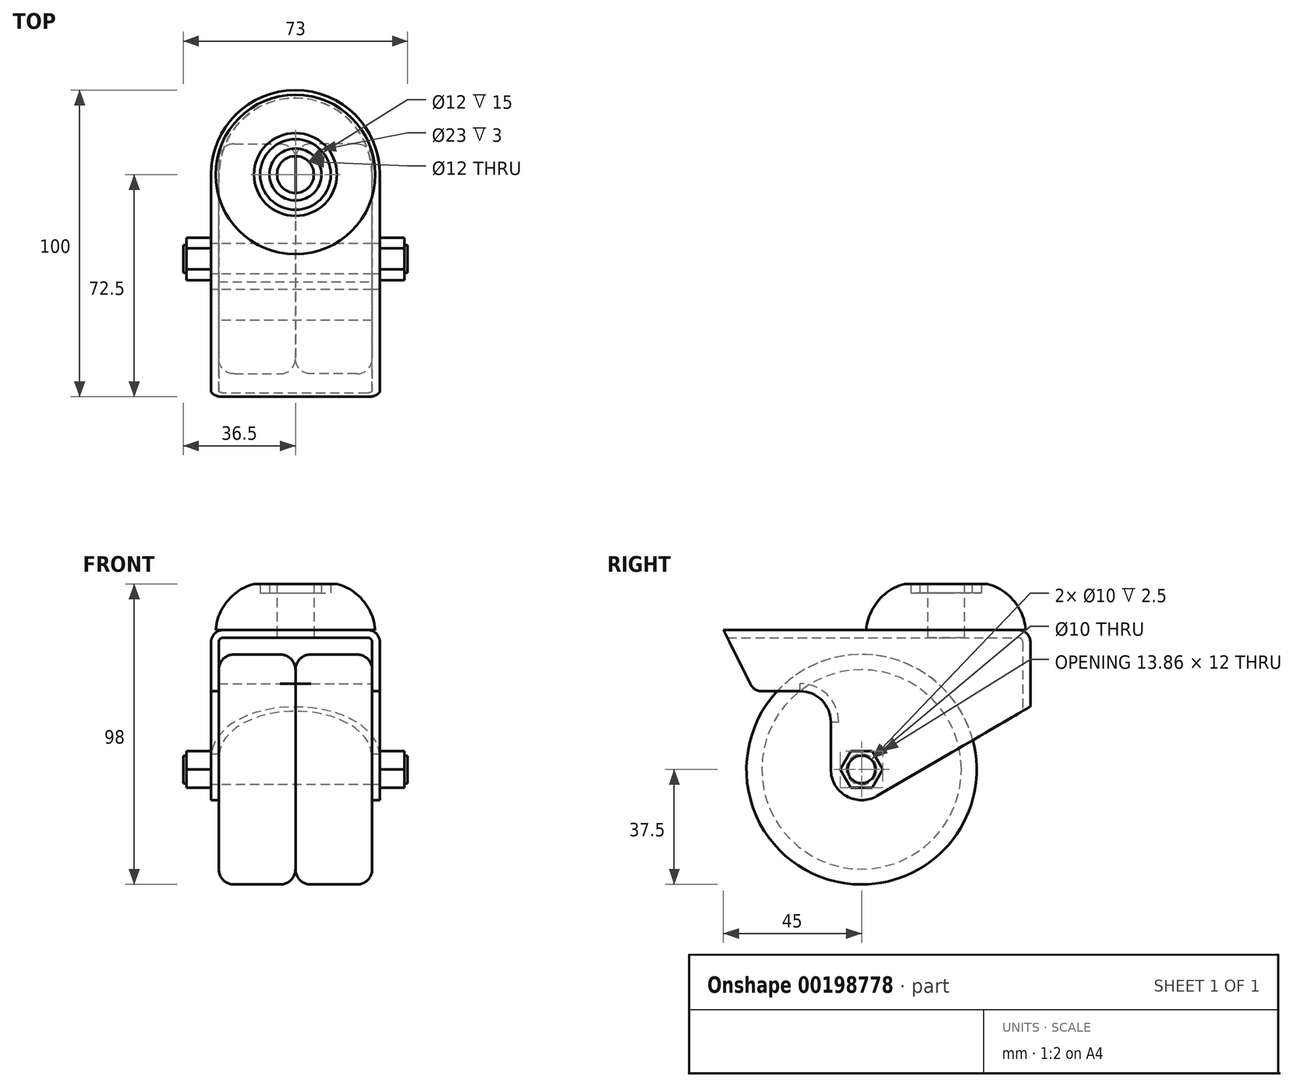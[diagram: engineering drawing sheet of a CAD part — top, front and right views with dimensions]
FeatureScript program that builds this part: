
annotation { "Feature Type Name" : "Feature", "Feature Type Description" : "" }
export const myFeature = defineFeature(function(context is Context, id is Id, definition is map)
    precondition{}
    {
        {
            var Q0;
            Q0=qCreatedBy(makeId("Right.planeOp"),FACE);
            var sketch = newSketch(context, id + "F0", { "sketchPlane" : qUnion([Q0])});
            skCircle(sketch, "E0", {"center": v(0, 0) * mm, "radius": 37.5 * mm});
            skCircle(sketch, "E1", {"center": v(0, 0) * mm, "radius": 5 * mm});
            skSolve(sketch);
        }
        {
            var Q0;
            Q0=qSketchRegion(id+"F0",true);
            extrude(context, id + "F1", {"entities" : qUnion([Q0]), "depth" : 25 * mm});
        }
        {
            var Q0;
            Q0=makeQuery(id+"F1.opExtrude","CAP_EDGE",EDGE,{"disambiguationData":[OSD([sQuery(id+"F0.wireOp",EDGE,"E0")])],"isStart":true});
            var Q1;
            Q1=makeQuery(id+"F1.opExtrude","CAP_EDGE",EDGE,{"disambiguationData":[OSD([sQuery(id+"F0.wireOp",EDGE,"E0")])],"isStart":false});
            fillet(context, id + "F2", {"entities" : qUnion([Q0, Q1]), "radius" : 5 * mm, "tangentPropagation" : true, "allowEdgeOverflow" : false});
        }
        {
            var Q0;
            Q0=makeQuery(id+"F1.opExtrude","SWEPT_BODY",BODY,{"disambiguationData":[OSD([sQuery(id+"F0.wireOp",EDGE,"E0")])]});
            var Q1;
            Q1=qCreatedBy(makeId("Right.planeOp"),FACE);
            mirror(context, id + "F3", {"operationType" : NewBodyOperationType.ADD, "entities" : qUnion([Q0]), "mirrorPlane" : qUnion([Q1])});
        }
        {
            var Q0;
            Q0=qCreatedBy(makeId("Right.planeOp"),FACE);
            var sketch = newSketch(context, id + "F4", { "sketchPlane" : qUnion([Q0])});
            skCircle(sketch, "E2.0", {"center": v(0, 0) * mm, "radius": 5 * mm});
            skArc(sketch, "E3", {"start": v(-10, 0) * mm, "mid": v(-4.98, -8.67) * mm, "end": v(5.04, -8.64) * mm});
            skLineSegment(sketch, "E4", {"start": v(0, -37.5) * mm, "end": v(0, 45.5) * mm, "construction": true});
            skLineSegment(sketch, "E5", {"start": v(-45, 45.5) * mm, "end": v(55, 45.5) * mm});
            skLineSegment(sketch, "E6", {"start": v(-10, 0) * mm, "end": v(-10, 25.5) * mm});
            skLineSegment(sketch, "E7", {"start": v(-10, 25.5) * mm, "end": v(-35, 25.5) * mm});
            skLineSegment(sketch, "E8", {"start": v(-35, 25.5) * mm, "end": v(-45, 45.5) * mm});
            skLineSegment(sketch, "E9", {"start": v(5.04, -8.64) * mm, "end": v(55, 20.5) * mm});
            skLineSegment(sketch, "E10", {"start": v(55, 20.5) * mm, "end": v(55, 45.5) * mm});
            skSolve(sketch);
        }
        {
            var Q0;
            Q0=qSketchRegion(id+"F4",true);
            extrude(context, id + "F5", {"entities" : qUnion([Q0]), "depth" : 55 * mm, "symmetric" : true});
        }
        {
            var Q0;
            Q0=makeQuery(id+"F5.opExtrude","CAP_EDGE",EDGE,{"disambiguationData":[OSD([sQuery(id+"F4.wireOp",EDGE,"E10")])],"isStart":false});
            var Q1;
            Q1=makeQuery(id+"F5.opExtrude","CAP_EDGE",EDGE,{"disambiguationData":[OSD([sQuery(id+"F4.wireOp",EDGE,"E10")])],"isStart":true});
            fillet(context, id + "F6", {"entities" : qUnion([Q0, Q1]), "radius" : (55 / 2) * mm, "tangentPropagation" : true, "allowEdgeOverflow" : false});
        }
        {
            var Q0;
            Q0=makeQuery(id+"F5.opExtrude","SWEPT_EDGE",EDGE,{"disambiguationData":[OSD([sQuery(id+"F4.wireOp",EDGE,"E6"),sQuery(id+"F4.wireOp",EDGE,"E7")])]});
            fillet(context, id + "F7", {"entities" : qUnion([Q0]), "radius" : 10 * mm, "tangentPropagation" : true, "allowEdgeOverflow" : false});
        }
        {
            var Q0;
            Q0=makeQuery(id+"F5.opExtrude","CAP_EDGE",EDGE,{"disambiguationData":[OSD([sQuery(id+"F4.wireOp",EDGE,"E5")])],"isStart":false});
            var Q1;
            Q1=makeQuery(id+"F5.opExtrude","SWEPT_EDGE",EDGE,{"disambiguationData":[OSD([sQuery(id+"F4.wireOp",EDGE,"E7"),sQuery(id+"F4.wireOp",EDGE,"E8")])]});
            fillet(context, id + "F8", {"entities" : qUnion([Q0, Q1]), "radius" : 4 * mm, "tangentPropagation" : true, "allowEdgeOverflow" : false});
        }
        {
            var Q0;
            Q0=makeQuery(id+"F5.opExtrude","SWEPT_FACE",FACE,{"disambiguationData":[OSD([sQuery(id+"F4.wireOp",EDGE,"E8")])]});
            var Q1;
            Q1=makeQuery(id+"F8.opFillet","BLEND_FACE",FACE,{"disambiguationData":[OSD([sQuery(id+"F4.wireOp",EDGE,"E7"),sQuery(id+"F4.wireOp",EDGE,"E8")])]});
            var Q2;
            Q2=makeQuery(id+"F5.opExtrude","SWEPT_FACE",FACE,{"disambiguationData":[OSD([sQuery(id+"F4.wireOp",EDGE,"E7")])]});
            var Q3;
            Q3=makeQuery(id+"F5.opExtrude","SWEPT_FACE",FACE,{"disambiguationData":[OSD([sQuery(id+"F4.wireOp",EDGE,"E6")])]});
            var Q4;
            Q4=makeQuery(id+"F5.opExtrude","SWEPT_FACE",FACE,{"disambiguationData":[OSD([sQuery(id+"F4.wireOp",EDGE,"E3")])]});
            var Q5;
            Q5=makeQuery(id+"F5.opExtrude","SWEPT_FACE",FACE,{"disambiguationData":[OSD([sQuery(id+"F4.wireOp",EDGE,"E2.0")])]});
            var Q6;
            Q6=makeQuery(id+"F5.opExtrude","SWEPT_FACE",FACE,{"disambiguationData":[OSD([sQuery(id+"F4.wireOp",EDGE,"E9")])]});
            shell(context, id + "F9", {"entities" : qUnion([Q0, Q1, Q2, Q3, Q4, Q5, Q6]), "thickness" : 2.5 * mm});
        }
        {
            var Q0;
            Q0=qCreatedBy(makeId("Right.planeOp"),FACE);
            var sketch = newSketch(context, id + "F10", { "sketchPlane" : qUnion([Q0])});
            skLineSegment(sketch, "E11.0", {"start": v(27.5, 45.5) * mm, "end": v(51, 45.5) * mm, "construction": true});
            skLineSegment(sketch, "E12", {"start": v(27.5, 45.5) * mm, "end": v(27.5, 60.5) * mm, "construction": true});
            skLineSegment(sketch, "E13.0", {"start": v(33.5, 45.5) * mm, "end": v(33.5, 60.5) * mm});
            skLineSegment(sketch, "E14", {"start": v(33.5, 60.5) * mm, "end": v(36, 60.5) * mm});
            skLineSegment(sketch, "E15", {"start": v(36, 60.5) * mm, "end": v(36, 57.5) * mm});
            skLineSegment(sketch, "E16", {"start": v(36, 57.5) * mm, "end": v(39, 57.5) * mm});
            skLineSegment(sketch, "E17", {"start": v(39, 57.5) * mm, "end": v(39, 60.5) * mm});
            skLineSegment(sketch, "E18", {"start": v(39, 60.5) * mm, "end": v(41, 60.5) * mm});
            skLineSegment(sketch, "E19", {"start": v(33.5, 45.5) * mm, "end": v(53.5, 45.5) * mm});
            skArc(sketch, "E20", {"start": v(53.5, 45.5) * mm, "mid": v(49.62, 54.97) * mm, "end": v(41, 60.5) * mm});
            skSolve(sketch);
        }
        {
            var Q0;
            Q0=makeQuery(id+"F10.imprint","IMPRINT",FACE,{"disambiguationData":[TD([[makeQuery(id+"F10.imprint","IMPRINT",EDGE,{"derivedFrom":sQuery(id+"F10.wireOp",EDGE,"E13.0")}),-1.0]])]});
            var Q1;
            Q1=sQuery(id+"F10.wireOp",EDGE,"E12");
            revolve(context, id + "F11", {"entities" : qUnion([Q0]), "axis" : qUnion([Q1]), "revolveType" : RevolveType.FULL});
        }
        {
            var Q0;
            {var subQ0=sQuery(id+"F4.wireOp",EDGE,"E5");Q0=makeQuery(id+"F9.opShell","OFFSET_FACE",FACE,{"disambiguationData":[OSD([subQ0]),TDD([makeQuery(id+"F5.opExtrude","SWEPT_FACE",FACE,{"disambiguationData":[OSD([subQ0])]})])]});}
            var sketch = newSketch(context, id + "F12", { "sketchPlane" : qUnion([Q0])});
            skCircle(sketch, "E21.0", {"center": v(0, -27.5) * mm, "radius": 6 * mm});
            skSolve(sketch);
        }
        {
            var Q0;
            Q0=qSketchRegion(id+"F12",true);
            extrude(context, id + "F13", {"entities" : qUnion([Q0]), "operationType" : NewBodyOperationType.REMOVE, "oppositeDirection" : true, "depth" : 43.9 * mm});
        }
        {
            var Q0;
            Q0=makeQuery(id+"F5.opExtrude","CAP_FACE",FACE,{"disambiguationData":[OSD([sQuery(id+"F4.wireOp",EDGE,"E2.0"),sQuery(id+"F4.wireOp",EDGE,"E3"),sQuery(id+"F4.wireOp",EDGE,"E5"),sQuery(id+"F4.wireOp",EDGE,"E6"),sQuery(id+"F4.wireOp",EDGE,"E7"),sQuery(id+"F4.wireOp",EDGE,"E8"),sQuery(id+"F4.wireOp",EDGE,"E9"),sQuery(id+"F4.wireOp",EDGE,"E10")])],"isStart":false});
            var sketch = newSketch(context, id + "F14", { "sketchPlane" : qUnion([Q0])});
            skCircle(sketch, "E22.0", {"center": v(0, 0) * mm, "radius": 5 * mm, "construction": true});
            skCircle(sketch, "E23.cCircle", {"center": v(0, 0) * mm, "radius": 6 * mm, "construction": true});
            skLineSegment(sketch, "E23.0", {"start": v(-3.46, 6) * mm, "end": v(3.46, 6) * mm});
            skLineSegment(sketch, "E23.1", {"start": v(3.46, 6) * mm, "end": v(6.93, 0) * mm});
            skLineSegment(sketch, "E23.2", {"start": v(6.93, 0) * mm, "end": v(3.46, -6) * mm});
            skLineSegment(sketch, "E23.3", {"start": v(3.46, -6) * mm, "end": v(-3.46, -6) * mm});
            skLineSegment(sketch, "E23.4", {"start": v(-3.46, -6) * mm, "end": v(-6.93, 0) * mm});
            skLineSegment(sketch, "E23.5", {"start": v(-6.93, 0) * mm, "end": v(-3.46, 6) * mm});
            skPoint(sketch, "E23.0.midPoint", {"position": v(0, 6) * mm});
            skSolve(sketch);
        }
        {
            var Q0;
            Q0=qSketchRegion(id+"F14",true);
            extrude(context, id + "F15", {"entities" : qUnion([Q0]), "depth" : 8 * mm});
        }
        {
            var Q0;
            Q0=makeQuery(id+"F15.opExtrude","CAP_FACE",FACE,{"disambiguationData":[OSD([sQuery(id+"F14.wireOp",EDGE,"E23.0"),sQuery(id+"F14.wireOp",EDGE,"E23.1"),sQuery(id+"F14.wireOp",EDGE,"E23.2"),sQuery(id+"F14.wireOp",EDGE,"E23.3"),sQuery(id+"F14.wireOp",EDGE,"E23.4"),sQuery(id+"F14.wireOp",EDGE,"E23.5")])],"isStart":false});
            var sketch = newSketch(context, id + "F16", { "sketchPlane" : qUnion([Q0])});
            skCircle(sketch, "E24", {"center": v(0, 0) * mm, "radius": 4.5 * mm});
            skSolve(sketch);
        }
        {
            var Q0;
            Q0=qSketchRegion(id+"F16",true);
            extrude(context, id + "F17", {"entities" : qUnion([Q0]), "operationType" : NewBodyOperationType.ADD, "depth" : 1 * mm});
        }
        {
            var Q0;
            Q0=makeQuery(id+"F15.opExtrude","SWEPT_BODY",BODY,{"disambiguationData":[OSD([sQuery(id+"F14.wireOp",EDGE,"E23.0"),sQuery(id+"F14.wireOp",EDGE,"E23.1"),sQuery(id+"F14.wireOp",EDGE,"E23.2"),sQuery(id+"F14.wireOp",EDGE,"E23.3"),sQuery(id+"F14.wireOp",EDGE,"E23.4"),sQuery(id+"F14.wireOp",EDGE,"E23.5")])]});
            var Q1;
            Q1=qCreatedBy(makeId("Right.planeOp"),FACE);
            mirror(context, id + "F18", {"operationType" : NewBodyOperationType.ADD, "entities" : qUnion([Q0]), "mirrorPlane" : qUnion([Q1])});
        }
    });
